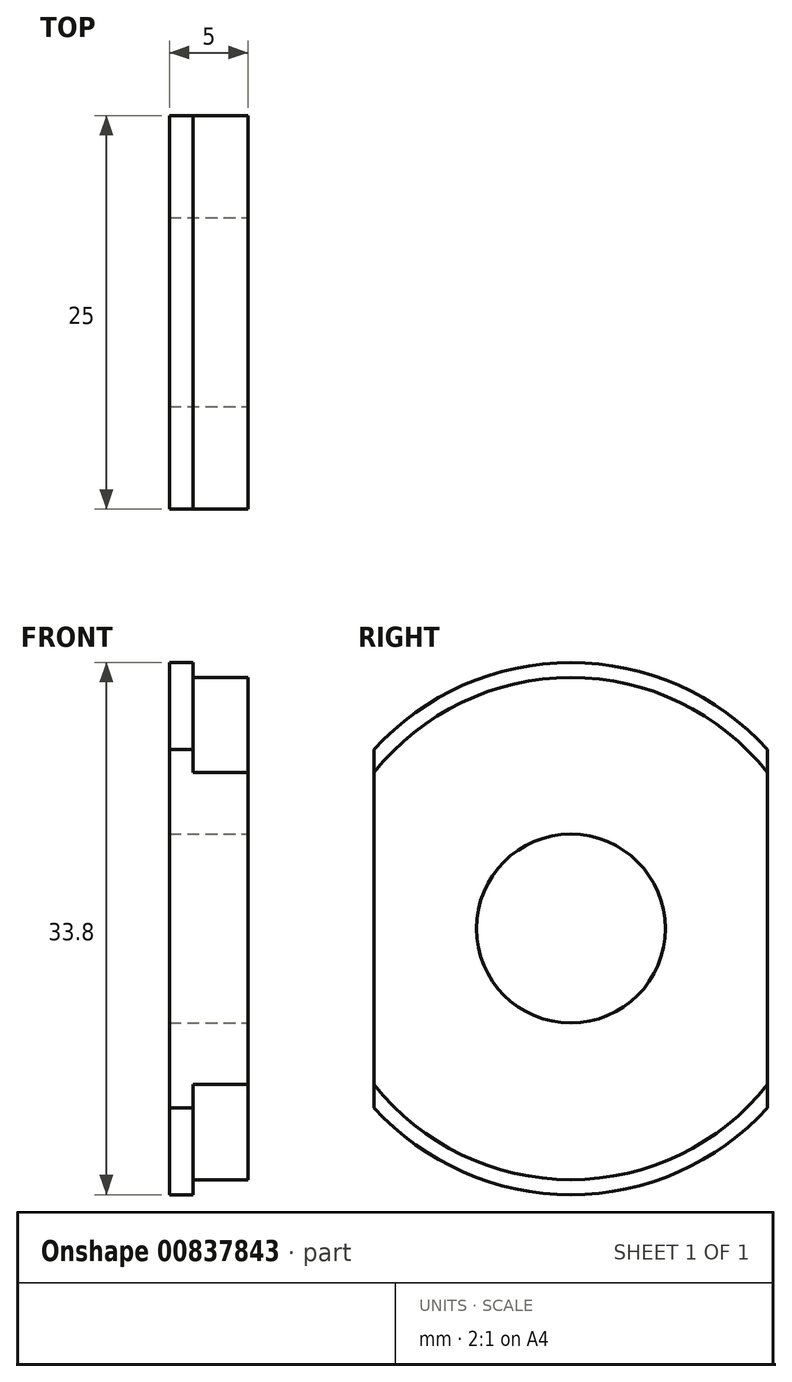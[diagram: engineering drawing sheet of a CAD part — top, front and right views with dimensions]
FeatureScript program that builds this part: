
annotation { "Feature Type Name" : "Feature", "Feature Type Description" : "" }
export const myFeature = defineFeature(function(context is Context, id is Id, definition is map)
    precondition{}
    {
        {
            var Q0;
            Q0=qCreatedBy(makeId("Front.planeOp"),FACE);
            var sketch = newSketch(context, id + "F0", { "sketchPlane" : qUnion([Q0])});
            skLineSegment(sketch, "E0", {"start": v(0, 0) * mm, "end": v(0, 16.9) * mm});
            skLineSegment(sketch, "E1", {"start": v(0, 16.9) * mm, "end": v(1.5, 16.9) * mm});
            skLineSegment(sketch, "E2", {"start": v(1.5, 16.9) * mm, "end": v(1.5, 15.95) * mm});
            skLineSegment(sketch, "E3", {"start": v(1.5, 15.95) * mm, "end": v(5, 15.95) * mm});
            skLineSegment(sketch, "E4", {"start": v(5, 15.95) * mm, "end": v(5, 0) * mm});
            skLineSegment(sketch, "E5", {"start": v(0, 0) * mm, "end": v(5, 0) * mm});
            skSolve(sketch);
        }
        {
            var Q0;
            Q0=makeQuery(id+"F0.imprint","IMPRINT",FACE,{"disambiguationData":[TD([[makeQuery(id+"F0.imprint","IMPRINT",EDGE,{"derivedFrom":sQuery(id+"F0.wireOp",EDGE,"E0")}),-1.0]])]});
            var Q1;
            Q1=sQuery(id+"F0.wireOp",EDGE,"E5");
            revolve(context, id + "F1", {"surfaceOperationType" : NewSurfaceOperationType.NEW, "entities" : qUnion([Q0]), "axis" : qUnion([Q1]), "revolveType" : RevolveType.FULL});
        }
        {
            var Q0;
            Q0=makeQuery(id+"F1.opRevolve","SWEPT_FACE",FACE,{"disambiguationData":[OSD([sQuery(id+"F0.wireOp",EDGE,"E4")])]});
            var sketch = newSketch(context, id + "F2", { "sketchPlane" : qUnion([Q0])});
            skPoint(sketch, "E6.0", {"position": v(0, 0) * mm});
            skSolve(sketch);
        }
        {
            var Q0;
            Q0=sQuery(id+"F2.wireOp",VERTEX,"E6.0");
            var Q1;
            Q1=makeQuery(id+"F1.opRevolve","SWEPT_BODY",BODY,{"disambiguationData":[OSD([sQuery(id+"F0.wireOp",EDGE,"E0"),sQuery(id+"F0.wireOp",EDGE,"E1"),sQuery(id+"F0.wireOp",EDGE,"E2"),sQuery(id+"F0.wireOp",EDGE,"E3"),sQuery(id+"F0.wireOp",EDGE,"E4"),sQuery(id+"F0.wireOp",EDGE,"E5")])]});
            hole(context, id + "F3", {"style" : HoleStyle.SIMPLE, "endStyle" : HoleEndStyle.THROUGH, "holeDiameter" : 12 * mm, "majorDiameter" : 5 * mm, "isTappedThrough" : true, "tappedDepth" : 12 * mm, "tapClearance" : 3, "locations" : qUnion([Q0]), "scope" : qUnion([Q1])});
        }
        {
            var Q0;
            Q0=makeQuery(id+"F1.opRevolve","SWEPT_FACE",FACE,{"disambiguationData":[OSD([sQuery(id+"F0.wireOp",EDGE,"E4")])]});
            var sketch = newSketch(context, id + "F4", { "sketchPlane" : qUnion([Q0])});
            skCircle(sketch, "E7.0", {"center": v(0, 0) * mm, "radius": 16.9 * mm});
            skLineSegment(sketch, "E8.left", {"start": v(-12.5, 11.37) * mm, "end": v(-12.5, -11.37) * mm});
            skLineSegment(sketch, "E8.right", {"start": v(12.5, 11.37) * mm, "end": v(12.5, -11.37) * mm});
            skSolve(sketch);
        }
        {
            var Q0;
            {var subQ0=sQuery(id+"F4.wireOp",EDGE,"E8.left");var subQ1=makeQuery(id+"F1.opRevolve","SWEPT_EDGE",EDGE,{"disambiguationData":[OSD([sQuery(id+"F0.wireOp",EDGE,"E3"),sQuery(id+"F0.wireOp",EDGE,"E4")])]});var subQ2=makeQuery(id+"F4.imprint","INTERSECT",VERTEX,{"disambiguationData":[OD(0.0)],"derivedFrom":[subQ1,subQ0]});Q0=makeQuery(id+"F4.imprint","IMPRINT",FACE,{"disambiguationData":[TD([[makeQuery(id+"F4.imprint","IMPRINT",EDGE,{"disambiguationData":[TD([[subQ2,-1.0]])],"derivedFrom":subQ0}),-1.0]])]});}
            var Q1;
            {var subQ0=sQuery(id+"F4.wireOp",EDGE,"E8.left");var subQ1=sQuery(id+"F4.wireOp",EDGE,"E7.0");var subQ2=makeQuery(id+"F4.imprint","INTERSECT",VERTEX,{"disambiguationData":[OD(0.0)],"derivedFrom":[subQ1,subQ0]});Q1=makeQuery(id+"F4.imprint","IMPRINT",FACE,{"disambiguationData":[TD([[makeQuery(id+"F4.imprint","IMPRINT",EDGE,{"disambiguationData":[TD([[subQ2,-1.0]])],"derivedFrom":subQ1}),1.0]])]});}
            var Q2;
            {var subQ0=sQuery(id+"F4.wireOp",EDGE,"E8.right");var subQ1=makeQuery(id+"F1.opRevolve","SWEPT_EDGE",EDGE,{"disambiguationData":[OSD([sQuery(id+"F0.wireOp",EDGE,"E3"),sQuery(id+"F0.wireOp",EDGE,"E4")])]});var subQ2=makeQuery(id+"F4.imprint","INTERSECT",VERTEX,{"disambiguationData":[OD(0.0)],"derivedFrom":[subQ1,subQ0]});Q2=makeQuery(id+"F4.imprint","IMPRINT",FACE,{"disambiguationData":[TD([[makeQuery(id+"F4.imprint","IMPRINT",EDGE,{"disambiguationData":[TD([[subQ2,-1.0]])],"derivedFrom":subQ0}),1.0]])]});}
            var Q3;
            {var subQ0=sQuery(id+"F4.wireOp",EDGE,"E8.right");var subQ1=sQuery(id+"F4.wireOp",EDGE,"E7.0");var subQ2=makeQuery(id+"F4.imprint","INTERSECT",VERTEX,{"disambiguationData":[OD(0.0)],"derivedFrom":[subQ1,subQ0]});Q3=makeQuery(id+"F4.imprint","IMPRINT",FACE,{"disambiguationData":[TD([[makeQuery(id+"F4.imprint","IMPRINT",EDGE,{"disambiguationData":[TD([[subQ2,1.0]])],"derivedFrom":subQ1}),1.0]])]});}
            extrude(context, id + "F5", {"entities" : qUnion([Q0, Q1, Q2, Q3]), "operationType" : NewBodyOperationType.REMOVE, "oppositeDirection" : true, "depth" : 25 * mm, "offsetDistance" : 25 * mm});
        }
    });
